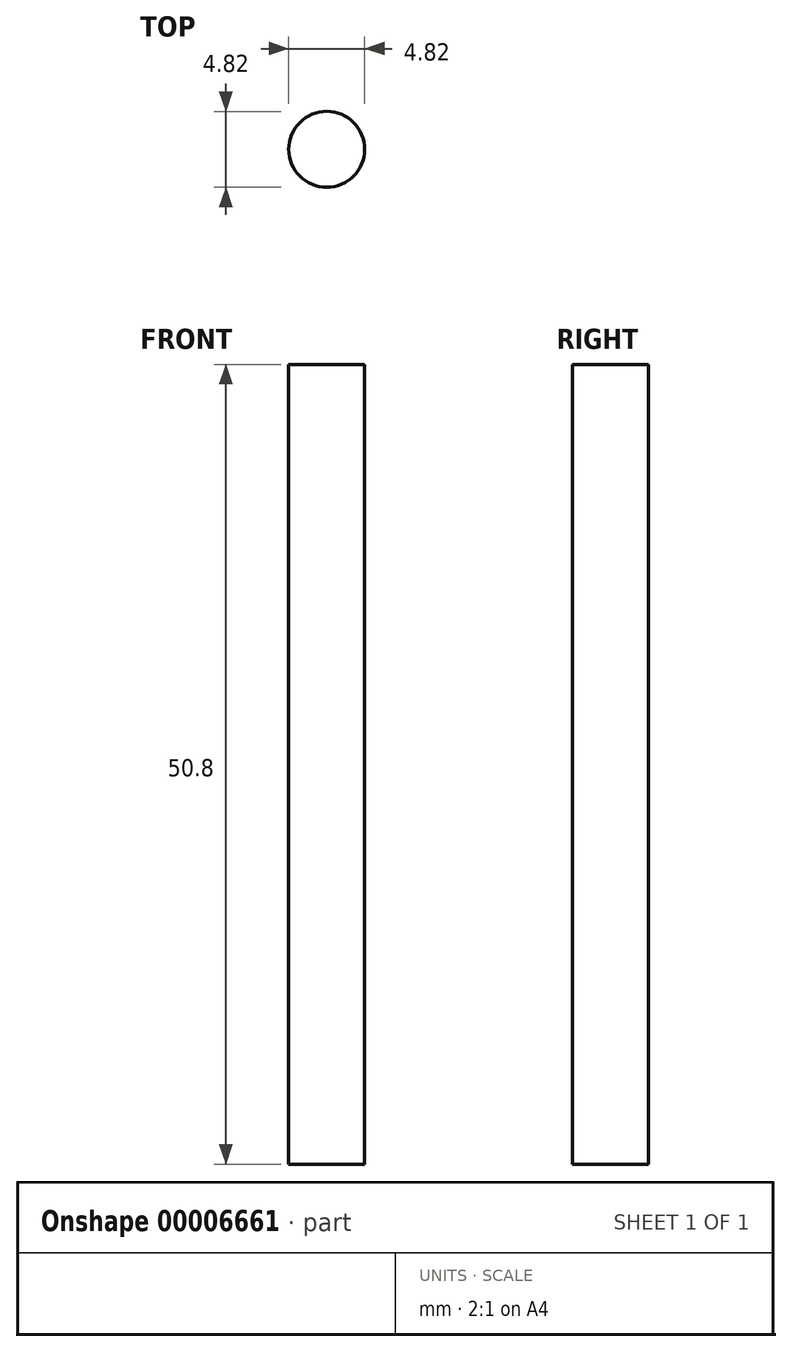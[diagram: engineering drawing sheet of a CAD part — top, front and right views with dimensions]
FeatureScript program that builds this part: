
annotation { "Feature Type Name" : "Feature", "Feature Type Description" : "" }
export const myFeature = defineFeature(function(context is Context, id is Id, definition is map)
    precondition{}
    {
        {
            var Q0;
            Q0=qCreatedBy(makeId("Top.planeOp"),FACE);
            var sketch = newSketch(context, id + "F0", { "sketchPlane" : qUnion([Q0])});
            skCircle(sketch, "E0", {"center": v(0, 0) * mm, "radius": 2.41 * mm});
            skSolve(sketch);
        }
        {
            var Q0;
            Q0 = qSketchRegion(id + "F0", true);
            extrude(context, id + "F1", {"entities" : qUnion([Q0]), "depth" : 50.8 * mm});
        }
    });
